# Revit family: Plumbing_Fixture-Grohe- Eurocube-Bath_Spout-12-METRIC
name_source: partatom
category: Plumbing Fixtures
revit_build: Autodesk Revit Architecture 2012 (Build: 20110916_2132(x64)
units: mm (PartAtom-declared; Revit-internal decimal feet)

## types (1)
- Eurocube 13 303 000
    ADA Compliant = Yes
    Assembly Code = C1030220
    AssetType = Fixed
    Barcode = 0
    CW Connection = Yes
    CWFU = 4.5
    Cold Water Connection Diameter = 10 mm  [stored 0.0328084 ft]
    Cold Water Radius = 5 mm  [stored 0.0164042 ft]
    Cost = 0 $
    Default Elevation = 600 mm
    Description = For a sharp, tailored look in your bathroom choose Eurocube. Here is a design so cleverly engineered that we are able to offer an extensive choice featuring true square design for the basin, bidet, shower and bath. Across the range, cut-out detailing on the lever handles reduces the perceived volume of each piece, while highlighting the minimalist appeal of the collection. Perfectly aligned to the design needs of today’s cosmopolitan consumers, Eurocube offers cutting-edge, geometric styling at an unbeatable price. At the same time it benefits from two leading GROHE technologies: GROHE SilkMove® – for smooth and comfortable operation of single lever mixers and GROHE StarLight® – our resilient chrome finish.
    Ecojoy = No
    ExpectedLife = 0
    Faucet Material = Grohe-Chrome
    HW Connection = Yes
    HWFU = 4.5
    Handle Spacing = 200 mm  [stored 0.656168 ft]
    Height = 60 mm  [stored 0.19685 ft]
    Hot Water Connection Diameter = 10 mm  [stored 0.0328084 ft]
    Hot Water Radius = 5 mm  [stored 0.0164042 ft]
    Keynote = N13
    Length = 193 mm  [stored 0.633202 ft]
    Low Emitting Material = Yes
    MaintenanceInformation = http://cdn08.grohe.com
    Manufacturer = Grohe AG
    Mixed Pipe Constraint = 80 mm  [stored 0.262467 ft]
    Mixed Pipe Length = 145 mm  [stored 0.475722 ft]
    Model = Eurocube 13 303 000
    ModelNumber = Eurocube 13 303 000
    Name = Eurocube 13 303 000
    Percentage of Recycled Content = 0
    Product Documentation Link = http://cdn08.grohe.com
    Product Page URL = http://www.grohe.com
    SerialNumber = 0
    Spare Parts List = http://cdn08.grohe.com
    SpareParts = Flow restrictor 6 l/min (13952 000), Seal (01282 00M)
    TagNumber = 0
    Type Comments = Bath spout, wall mounted.
    URL = www.grohe.com
    Vent Connection = No
    WFU = 0
    Waste Connection = No
    Width = 60 mm  [stored 0.19685 ft]
    _BIMspec_GUID = 0
    _current revision = 1
    _distributed by = www.bimstore.co.uk

note: [stored X ft] marks values corroborated as IEEE doubles in the binary element streams (Revit-internal decimal feet)

## geometry (parser evidence)
native form markers: Blend x2, Sweep x4
no freeform markers — native parametric forms only
